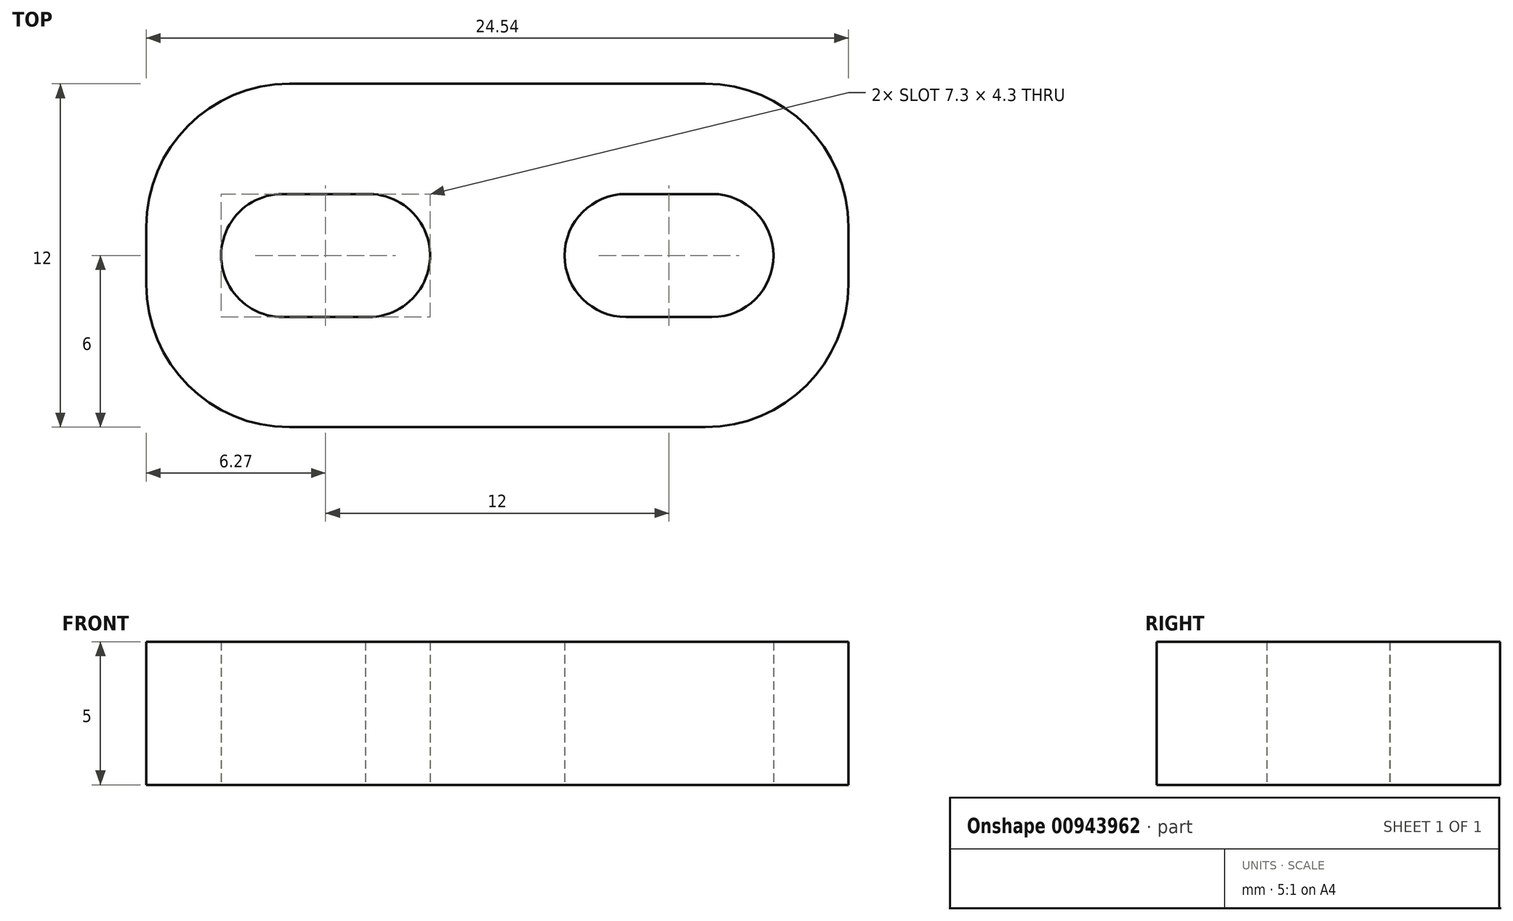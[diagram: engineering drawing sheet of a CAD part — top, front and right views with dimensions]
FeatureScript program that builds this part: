
annotation { "Feature Type Name" : "Feature", "Feature Type Description" : "" }
export const myFeature = defineFeature(function(context is Context, id is Id, definition is map)
    precondition{}
    {
        {
            var Q0;
            Q0=qCreatedBy(makeId("Top.planeOp"),FACE);
            var sketch = newSketch(context, id + "F0", { "sketchPlane" : qUnion([Q0])});
            skCircle(sketch, "E0", {"center": v(7.5, 0) * mm, "radius": 2.15 * mm});
            skCircle(sketch, "E1", {"center": v(-7.5, 0) * mm, "radius": 2.15 * mm});
            skCircle(sketch, "E2", {"center": v(-4.5, 0) * mm, "radius": 2.15 * mm});
            skCircle(sketch, "E3", {"center": v(4.5, 0) * mm, "radius": 2.15 * mm});
            skLineSegment(sketch, "E4", {"start": v(-7.49, -2.15) * mm, "end": v(-4.5, -2.15) * mm});
            skLineSegment(sketch, "E5", {"start": v(-7.5, 2.15) * mm, "end": v(-4.61, 2.15) * mm});
            skLineSegment(sketch, "E6", {"start": v(7.5, 2.15) * mm, "end": v(4.5, 2.15) * mm});
            skLineSegment(sketch, "E7", {"start": v(4.5, -2.15) * mm, "end": v(7.5, -2.15) * mm});
            skLineSegment(sketch, "E8.bottom", {"start": v(12.27, -6) * mm, "end": v(-12.27, -6) * mm});
            skLineSegment(sketch, "E8.top", {"start": v(12.27, 6) * mm, "end": v(-12.27, 6) * mm});
            skLineSegment(sketch, "E8.left", {"start": v(12.27, -6) * mm, "end": v(12.27, 6) * mm});
            skLineSegment(sketch, "E8.right", {"start": v(-12.27, -6) * mm, "end": v(-12.27, 6) * mm});
            skPoint(sketch, "E8.middle", {"position": v(0, 0) * mm});
            skSolve(sketch);
        }
        {
            var Q0;
            {var subQ7=sQuery(id+"F0.wireOp",EDGE,"E4");Q0=makeQuery(id+"F0.imprint","IMPRINT",FACE,{"disambiguationData":[TD([[makeQuery(id+"F0.imprint","IMPRINT",EDGE,{"derivedFrom":subQ7}),-1.0]])]});}
            extrude(context, id + "F1", {"entities" : qUnion([Q0]), "depth" : 5 * mm, "offsetDistance" : 25 * mm});
        }
        {
            var Q0;
            Q0=makeQuery(id+"F1.opExtrude","SWEPT_EDGE",EDGE,{"disambiguationData":[OSD([sQuery(id+"F0.wireOp",EDGE,"E8.top"),sQuery(id+"F0.wireOp",EDGE,"E8.left")])]});
            var Q1;
            Q1=makeQuery(id+"F1.opExtrude","SWEPT_EDGE",EDGE,{"disambiguationData":[OSD([sQuery(id+"F0.wireOp",EDGE,"E8.bottom"),sQuery(id+"F0.wireOp",EDGE,"E8.left")])]});
            var Q2;
            Q2=makeQuery(id+"F1.opExtrude","SWEPT_EDGE",EDGE,{"disambiguationData":[OSD([sQuery(id+"F0.wireOp",EDGE,"E8.bottom"),sQuery(id+"F0.wireOp",EDGE,"E8.right")])]});
            var Q3;
            Q3=makeQuery(id+"F1.opExtrude","SWEPT_EDGE",EDGE,{"disambiguationData":[OSD([sQuery(id+"F0.wireOp",EDGE,"E8.top"),sQuery(id+"F0.wireOp",EDGE,"E8.right")])]});
            fillet(context, id + "F2", {"entities" : qUnion([Q0, Q1, Q2, Q3]), "radius" : 5 * mm, "tangentPropagation" : true, "allowEdgeOverflow" : false});
        }
    });
